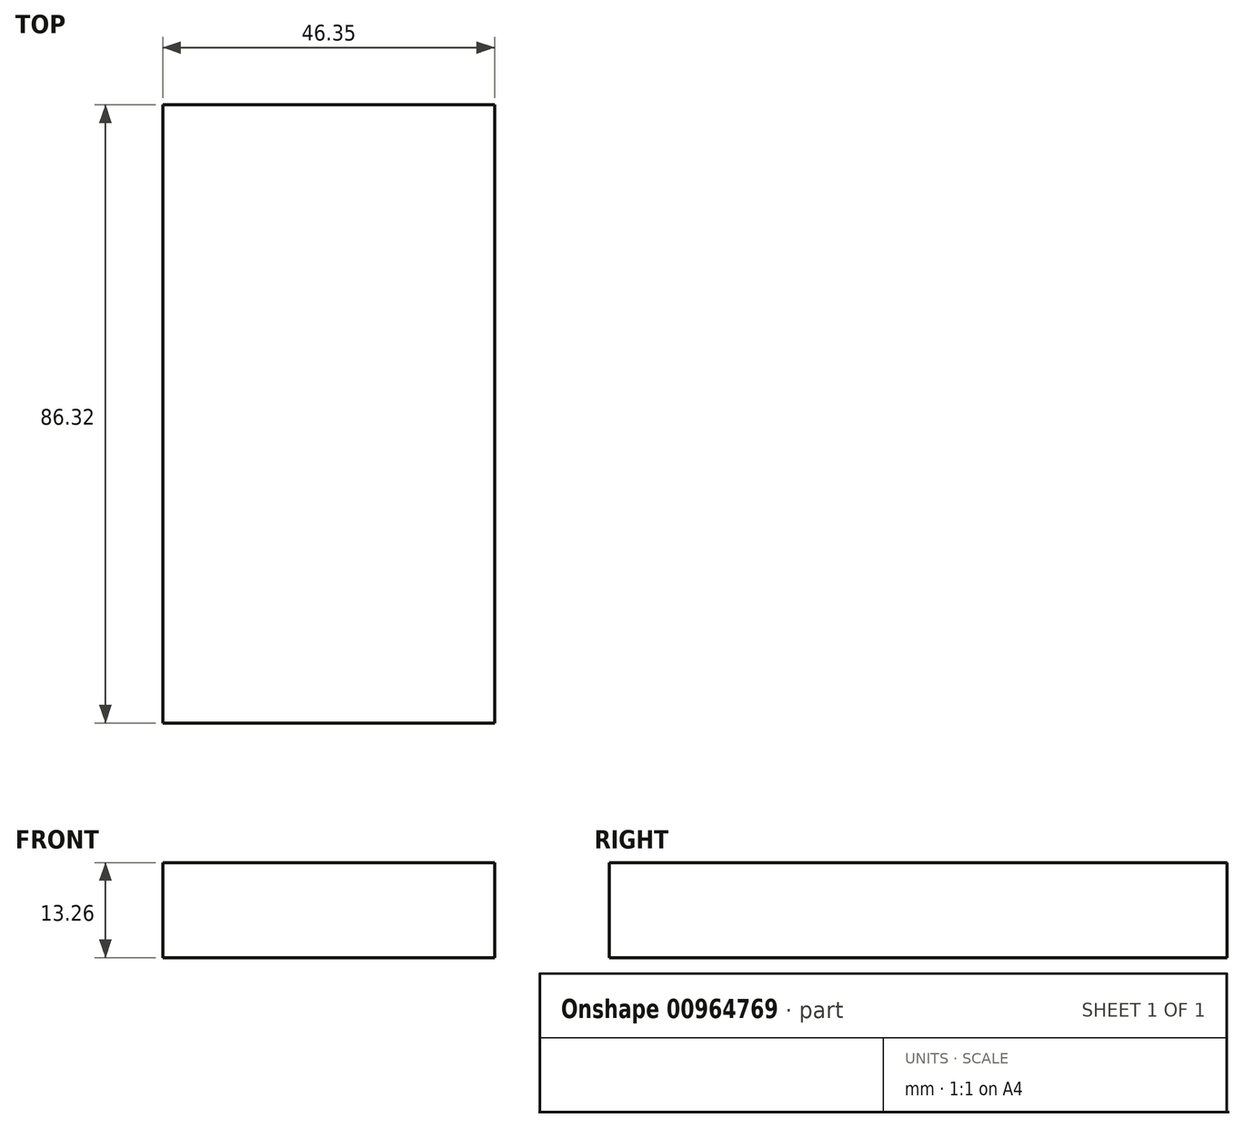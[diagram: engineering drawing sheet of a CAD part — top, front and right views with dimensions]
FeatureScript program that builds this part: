
annotation { "Feature Type Name" : "Feature", "Feature Type Description" : "" }
export const myFeature = defineFeature(function(context is Context, id is Id, definition is map)
    precondition{}
    {
        {
            var Q0;
            Q0=qCreatedBy(makeId("Right.planeOp"),FACE);
            var sketch = newSketch(context, id + "F0", { "sketchPlane" : qUnion([Q0])});
            skLineSegment(sketch, "E0", {"start": v(43.06, 13.26) * mm, "end": v(-43.26, 13.26) * mm});
            skLineSegment(sketch, "E1", {"start": v(-43.26, 13.26) * mm, "end": v(-43.26, 0) * mm});
            skLineSegment(sketch, "E2", {"start": v(-43.26, 0) * mm, "end": v(43.06, 0) * mm});
            skLineSegment(sketch, "E3", {"start": v(43.06, 0) * mm, "end": v(43.06, 13.26) * mm});
            skSolve(sketch);
        }
        {
            var Q0;
            Q0=makeQuery(id+"F0.imprint","IMPRINT",FACE,{"disambiguationData":[TD([[makeQuery(id+"F0.imprint","IMPRINT",EDGE,{"derivedFrom":sQuery(id+"F0.wireOp",EDGE,"E0")}),1.0]])]});
            extrude(context, id + "F1", {"entities" : qUnion([Q0]), "depth" : 46.35 * mm, "offsetDistance" : 25 * mm});
        }
    });
